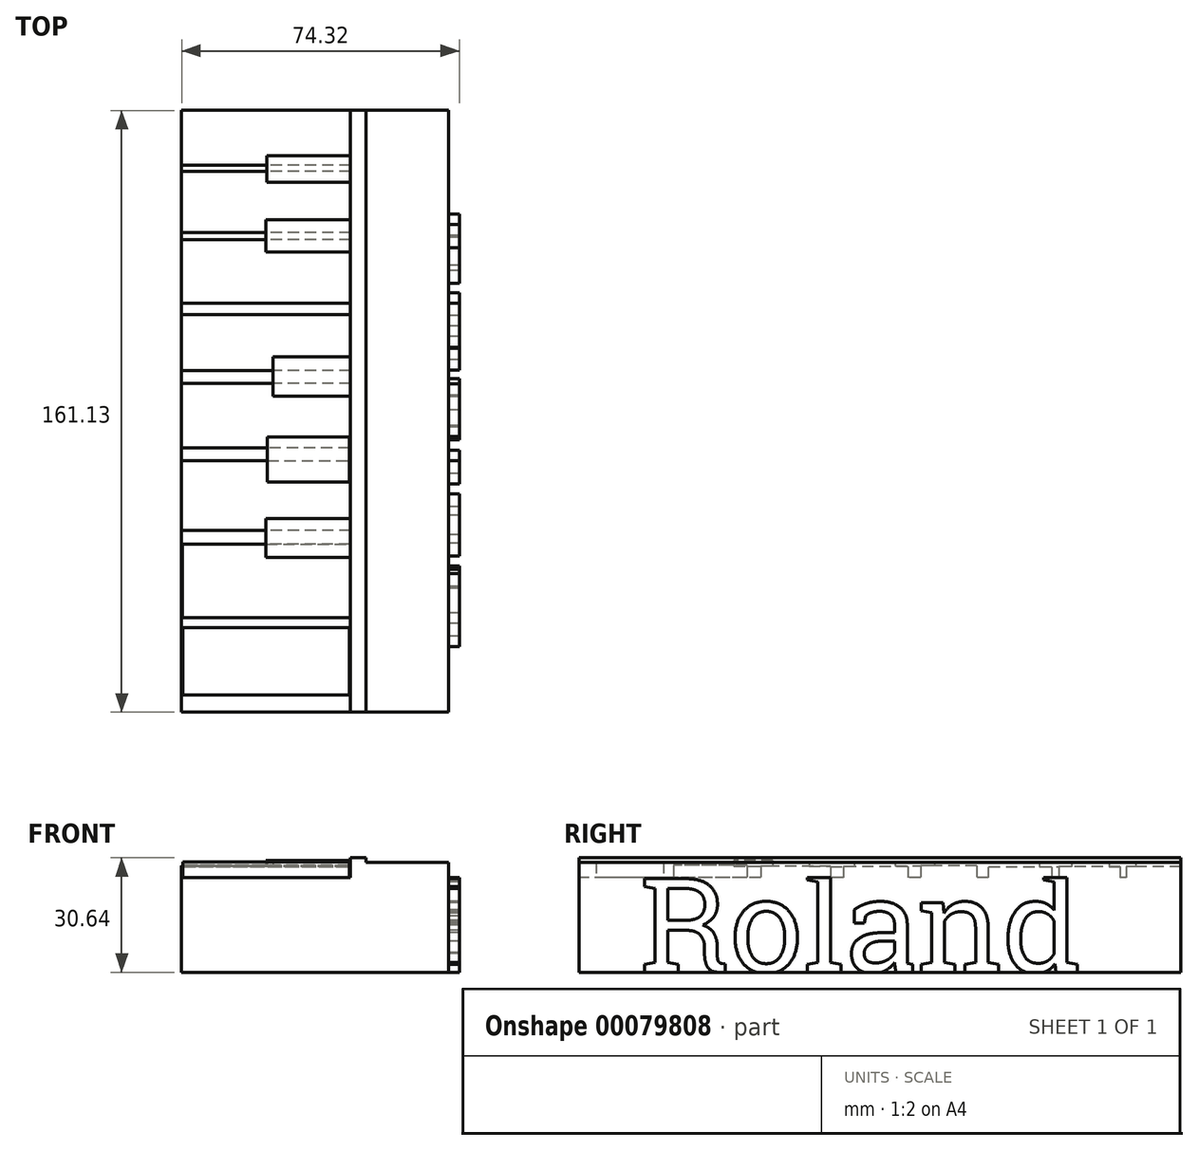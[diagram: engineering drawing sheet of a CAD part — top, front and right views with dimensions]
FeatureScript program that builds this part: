
annotation { "Feature Type Name" : "Feature", "Feature Type Description" : "" }
export const myFeature = defineFeature(function(context is Context, id is Id, definition is map)
    precondition{}
    {
        {
            var Q0;
            Q0=qCreatedBy(makeId("Top.planeOp"),FACE);
            var sketch = newSketch(context, id + "F0", { "sketchPlane" : qUnion([Q0])});
            skLineSegment(sketch, "E0.bottom", {"start": v(-39.3, 62.64) * mm, "end": v(32.17, 62.64) * mm});
            skLineSegment(sketch, "E0.top", {"start": v(-39.3, -98.49) * mm, "end": v(32.17, -98.49) * mm});
            skLineSegment(sketch, "E0.left", {"start": v(-39.3, 62.64) * mm, "end": v(-39.3, -98.49) * mm});
            skLineSegment(sketch, "E0.right", {"start": v(32.17, 62.64) * mm, "end": v(32.17, -98.49) * mm});
            skSolve(sketch);
        }
        {
            var Q0;
            Q0=makeQuery(id+"F0.imprint","IMPRINT",FACE,{"disambiguationData":[TD([[makeQuery(id+"F0.imprint","IMPRINT",EDGE,{"derivedFrom":sQuery(id+"F0.wireOp",EDGE,"E0.bottom")}),-1.0]])]});
            extrude(context, id + "F1", {"entities" : qUnion([Q0]), "depth" : 25.4 * mm});
        }
        {
            var Q0;
            Q0=makeQuery(id+"F1.opExtrude","CAP_FACE",FACE,{"disambiguationData":[OSD([sQuery(id+"F0.wireOp",EDGE,"E0.bottom"),sQuery(id+"F0.wireOp",EDGE,"E0.top"),sQuery(id+"F0.wireOp",EDGE,"E0.left"),sQuery(id+"F0.wireOp",EDGE,"E0.right")])],"isStart":false});
            var sketch = newSketch(context, id + "F2", { "sketchPlane" : qUnion([Q0])});
            skLineSegment(sketch, "E1.bottom", {"start": v(10.06, 62.64) * mm, "end": v(5.9, 62.64) * mm});
            skLineSegment(sketch, "E1.top", {"start": v(10.06, -98.49) * mm, "end": v(5.9, -98.49) * mm});
            skLineSegment(sketch, "E1.left", {"start": v(10.06, 62.64) * mm, "end": v(10.06, -98.49) * mm});
            skLineSegment(sketch, "E1.right", {"start": v(5.9, 62.64) * mm, "end": v(5.9, -98.49) * mm});
            skSolve(sketch);
        }
        {
            var Q0;
            Q0=makeQuery(id+"F2.imprint","IMPRINT",FACE,{"disambiguationData":[TD([[makeQuery(id+"F2.imprint","IMPRINT",EDGE,{"derivedFrom":sQuery(id+"F2.wireOp",EDGE,"E1.bottom")}),-1.0]])]});
            extrude(context, id + "F3", {"entities" : qUnion([Q0]), "operationType" : NewBodyOperationType.ADD, "depth" : 5.24 * mm});
        }
        {
            var Q0;
            {var subQ0=sQuery(id+"F0.wireOp",EDGE,"E0.left");var subQ1=sQuery(id+"F0.wireOp",EDGE,"E0.top");var subQ2=sQuery(id+"F0.wireOp",EDGE,"E0.bottom");Q0=makeQuery(id+"F3.boolean.opBoolean","SPLIT",FACE,{"disambiguationData":[TD([makeQuery(id+"F1.opExtrude","SWEPT_FACE",FACE,{"disambiguationData":[OSD([subQ0])]})])],"derivedFrom":makeQuery(id+"F1.opExtrude","CAP_FACE",FACE,{"disambiguationData":[OSD([subQ2,subQ1,subQ0,sQuery(id+"F0.wireOp",EDGE,"E0.right")])],"isStart":false})});}
            var sketch = newSketch(context, id + "F4", { "sketchPlane" : qUnion([Q0])});
            skLineSegment(sketch, "E2.bottom", {"start": v(5.9, 62.64) * mm, "end": v(-39.3, 62.64) * mm});
            skLineSegment(sketch, "E2.top", {"start": v(5.9, 47.98) * mm, "end": v(-39.3, 47.98) * mm});
            skLineSegment(sketch, "E2.left", {"start": v(5.9, 62.64) * mm, "end": v(5.9, 47.98) * mm});
            skLineSegment(sketch, "E2.right", {"start": v(-39.3, 62.64) * mm, "end": v(-39.3, 47.98) * mm});
            skSolve(sketch);
        }
        {
            var Q0;
            Q0=makeQuery(id+"F4.imprint","IMPRINT",FACE,{"disambiguationData":[TD([[makeQuery(id+"F4.imprint","IMPRINT",EDGE,{"derivedFrom":sQuery(id+"F4.wireOp",EDGE,"E2.bottom")}),-1.0]])]});
            extrude(context, id + "F5", {"entities" : qUnion([Q0]), "operationType" : NewBodyOperationType.ADD, "depth" : 2.9 * mm});
        }
        {
            var Q0;
            {var subQ0=sQuery(id+"F0.wireOp",EDGE,"E0.left");var subQ1=sQuery(id+"F0.wireOp",EDGE,"E0.top");var subQ2=sQuery(id+"F0.wireOp",EDGE,"E0.bottom");Q0=makeQuery(id+"F3.boolean.opBoolean","SPLIT",FACE,{"disambiguationData":[TD([makeQuery(id+"F1.opExtrude","SWEPT_FACE",FACE,{"disambiguationData":[OSD([subQ0])]})])],"derivedFrom":makeQuery(id+"F1.opExtrude","CAP_FACE",FACE,{"disambiguationData":[OSD([subQ2,subQ1,subQ0,sQuery(id+"F0.wireOp",EDGE,"E0.right")])],"isStart":false})});}
            var sketch = newSketch(context, id + "F6", { "sketchPlane" : qUnion([Q0])});
            skLineSegment(sketch, "E3.bottom", {"start": v(5.9, 46.37) * mm, "end": v(-39.3, 46.37) * mm});
            skLineSegment(sketch, "E3.top", {"start": v(5.9, 30) * mm, "end": v(-39.3, 30) * mm});
            skLineSegment(sketch, "E3.left", {"start": v(5.9, 46.37) * mm, "end": v(5.9, 30) * mm});
            skLineSegment(sketch, "E3.right", {"start": v(-39.3, 46.37) * mm, "end": v(-39.3, 30) * mm});
            skSolve(sketch);
        }
        {
            var Q0;
            Q0=makeQuery(id+"F6.imprint","IMPRINT",FACE,{"disambiguationData":[TD([[makeQuery(id+"F6.imprint","IMPRINT",EDGE,{"derivedFrom":sQuery(id+"F6.wireOp",EDGE,"E3.bottom")}),1.0]])]});
            extrude(context, id + "F7", {"entities" : qUnion([Q0]), "operationType" : NewBodyOperationType.ADD, "depth" : 2.86 * mm});
        }
        {
            var Q0;
            Q0=makeQuery(id+"F5.opExtrude","CAP_FACE",FACE,{"disambiguationData":[OSD([sQuery(id+"F4.wireOp",EDGE,"E2.bottom"),sQuery(id+"F4.wireOp",EDGE,"E2.top"),sQuery(id+"F4.wireOp",EDGE,"E2.left"),sQuery(id+"F4.wireOp",EDGE,"E2.right")])],"isStart":false});
            var sketch = newSketch(context, id + "F8", { "sketchPlane" : qUnion([Q0])});
            skLineSegment(sketch, "E4.bottom", {"start": v(5.9, 50.54) * mm, "end": v(-16.48, 50.54) * mm});
            skLineSegment(sketch, "E4.top", {"start": v(5.9, 43.8) * mm, "end": v(-16.48, 43.8) * mm});
            skLineSegment(sketch, "E4.left", {"start": v(5.9, 50.54) * mm, "end": v(5.9, 43.8) * mm});
            skLineSegment(sketch, "E4.right", {"start": v(-16.48, 50.54) * mm, "end": v(-16.48, 43.8) * mm});
            skSolve(sketch);
        }
        {
            var Q0;
            {var subQ0=sQuery(id+"F8.wireOp",EDGE,"E4.bottom");Q0=makeQuery(id+"F8.imprint","IMPRINT",FACE,{"disambiguationData":[TD([[makeQuery(id+"F8.imprint","IMPRINT",EDGE,{"derivedFrom":subQ0}),1.0]])]});}
            extrude(context, id + "F9", {"entities" : qUnion([Q0]), "operationType" : NewBodyOperationType.ADD, "depth" : 1 * mm});
        }
        {
            var Q0;
            {var subQ0=sQuery(id+"F4.wireOp",EDGE,"E2.top");Q0=makeQuery(id+"F9.boolean.opBoolean","MERGE",FACE,{"derivedFrom":[makeQuery(id+"F5.opExtrude","SWEPT_FACE",FACE,{"disambiguationData":[OSD([subQ0])]}),makeQuery(id+"F9.opExtrude","SWEPT_FACE",FACE,{"disambiguationData":[OSD([subQ0])]})]});}
            var sketch = newSketch(context, id + "F10", { "sketchPlane" : qUnion([Q0])});
            skLineSegment(sketch, "E5.bottom", {"start": v(5.9, 29.3) * mm, "end": v(-16.48, 29.3) * mm});
            skLineSegment(sketch, "E5.top", {"start": v(5.9, 28.3) * mm, "end": v(-16.48, 28.3) * mm});
            skLineSegment(sketch, "E5.left", {"start": v(5.9, 29.3) * mm, "end": v(5.9, 28.3) * mm});
            skLineSegment(sketch, "E5.right", {"start": v(-16.48, 29.3) * mm, "end": v(-16.48, 28.3) * mm});
            skSolve(sketch);
        }
        {
            var Q0;
            Q0=makeQuery(id+"F10.imprint","IMPRINT",FACE,{"disambiguationData":[TD([[makeQuery(id+"F10.imprint","IMPRINT",EDGE,{"derivedFrom":sQuery(id+"F10.wireOp",EDGE,"E5.bottom")}),1.0]])]});
            extrude(context, id + "F11", {"entities" : qUnion([Q0]), "operationType" : NewBodyOperationType.ADD, "depth" : 4.6 * mm});
        }
        {
            var Q0;
            {var subQ2=sQuery(id+"F0.wireOp",EDGE,"E0.left");var subQ3=makeQuery(id+"F1.opExtrude","SWEPT_FACE",FACE,{"disambiguationData":[OSD([subQ2])]});var subQ4=sQuery(id+"F0.wireOp",EDGE,"E0.top");var subQ5=makeQuery(id+"F1.opExtrude","SWEPT_FACE",FACE,{"disambiguationData":[OSD([subQ4])]});var subQ6=sQuery(id+"F0.wireOp",EDGE,"E0.bottom");Q0=makeQuery(id+"F7.boolean.opBoolean","SPLIT",FACE,{"disambiguationData":[TD([subQ5])],"derivedFrom":makeQuery(id+"F3.boolean.opBoolean","SPLIT",FACE,{"disambiguationData":[TD([subQ3])],"derivedFrom":makeQuery(id+"F1.opExtrude","CAP_FACE",FACE,{"disambiguationData":[OSD([subQ6,subQ4,subQ2,sQuery(id+"F0.wireOp",EDGE,"E0.right")])],"isStart":false})})});}
            var sketch = newSketch(context, id + "F12", { "sketchPlane" : qUnion([Q0])});
            skLineSegment(sketch, "E6.bottom", {"start": v(5.9, 28) * mm, "end": v(-39.3, 28) * mm});
            skLineSegment(sketch, "E6.top", {"start": v(5.9, 11.05) * mm, "end": v(-39.3, 11.05) * mm});
            skLineSegment(sketch, "E6.left", {"start": v(5.9, 28) * mm, "end": v(5.9, 11.05) * mm});
            skLineSegment(sketch, "E6.right", {"start": v(-39.3, 28) * mm, "end": v(-39.3, 11.05) * mm});
            skSolve(sketch);
        }
        {
            var Q0;
            Q0=makeQuery(id+"F12.imprint","IMPRINT",FACE,{"disambiguationData":[TD([[makeQuery(id+"F12.imprint","IMPRINT",EDGE,{"derivedFrom":sQuery(id+"F12.wireOp",EDGE,"E6.bottom")}),1.0]])]});
            extrude(context, id + "F13", {"entities" : qUnion([Q0]), "operationType" : NewBodyOperationType.ADD, "depth" : 2.72 * mm});
        }
        {
            var Q0;
            Q0=makeQuery(id+"F7.opExtrude","CAP_FACE",FACE,{"disambiguationData":[OSD([sQuery(id+"F6.wireOp",EDGE,"E3.bottom"),sQuery(id+"F6.wireOp",EDGE,"E3.top"),sQuery(id+"F6.wireOp",EDGE,"E3.left"),sQuery(id+"F6.wireOp",EDGE,"E3.right")])],"isStart":false});
            var sketch = newSketch(context, id + "F14", { "sketchPlane" : qUnion([Q0])});
            skLineSegment(sketch, "E7.bottom", {"start": v(5.9, 33.31) * mm, "end": v(-16.7, 33.31) * mm});
            skLineSegment(sketch, "E7.top", {"start": v(5.9, 30) * mm, "end": v(-16.7, 30) * mm});
            skLineSegment(sketch, "E7.left", {"start": v(5.9, 33.31) * mm, "end": v(5.9, 30) * mm});
            skLineSegment(sketch, "E7.right", {"start": v(-16.7, 33.31) * mm, "end": v(-16.7, 30) * mm});
            skSolve(sketch);
        }
        {
            var Q0;
            Q0=makeQuery(id+"F14.imprint","IMPRINT",FACE,{"disambiguationData":[TD([[makeQuery(id+"F14.imprint","IMPRINT",EDGE,{"derivedFrom":sQuery(id+"F14.wireOp",EDGE,"E7.bottom")}),1.0]])]});
            extrude(context, id + "F15", {"entities" : qUnion([Q0]), "operationType" : NewBodyOperationType.ADD, "depth" : 0.97 * mm});
        }
        {
            var Q0;
            Q0=makeQuery(id+"F15.boolean.opBoolean","MERGE",FACE,{"derivedFrom":[makeQuery(id+"F7.opExtrude","SWEPT_FACE",FACE,{"disambiguationData":[OSD([sQuery(id+"F6.wireOp",EDGE,"E3.top")])]}),makeQuery(id+"F15.opExtrude","SWEPT_FACE",FACE,{"disambiguationData":[OSD([sQuery(id+"F14.wireOp",EDGE,"E7.top")])]})]});
            var sketch = newSketch(context, id + "F16", { "sketchPlane" : qUnion([Q0])});
            skLineSegment(sketch, "E8.bottom", {"start": v(5.9, 29.23) * mm, "end": v(-16.7, 29.23) * mm});
            skLineSegment(sketch, "E8.top", {"start": v(5.9, 28.26) * mm, "end": v(-16.7, 28.26) * mm});
            skLineSegment(sketch, "E8.left", {"start": v(5.9, 29.23) * mm, "end": v(5.9, 28.26) * mm});
            skLineSegment(sketch, "E8.right", {"start": v(-16.7, 29.23) * mm, "end": v(-16.7, 28.26) * mm});
            skSolve(sketch);
        }
        {
            var Q0;
            Q0=makeQuery(id+"F16.imprint","IMPRINT",FACE,{"disambiguationData":[TD([[makeQuery(id+"F16.imprint","IMPRINT",EDGE,{"derivedFrom":sQuery(id+"F16.wireOp",EDGE,"E8.bottom")}),1.0]])]});
            extrude(context, id + "F17", {"entities" : qUnion([Q0]), "operationType" : NewBodyOperationType.ADD, "depth" : 5.23 * mm});
        }
        {
            var Q0;
            {var subQ3=sQuery(id+"F0.wireOp",EDGE,"E0.left");var subQ4=makeQuery(id+"F1.opExtrude","SWEPT_FACE",FACE,{"disambiguationData":[OSD([subQ3])]});var subQ6=sQuery(id+"F0.wireOp",EDGE,"E0.top");var subQ7=makeQuery(id+"F1.opExtrude","SWEPT_FACE",FACE,{"disambiguationData":[OSD([subQ6])]});var subQ8=sQuery(id+"F0.wireOp",EDGE,"E0.bottom");Q0=makeQuery(id+"F13.boolean.opBoolean","SPLIT",FACE,{"disambiguationData":[TD([subQ7])],"derivedFrom":makeQuery(id+"F7.boolean.opBoolean","SPLIT",FACE,{"disambiguationData":[TD([subQ7])],"derivedFrom":makeQuery(id+"F3.boolean.opBoolean","SPLIT",FACE,{"disambiguationData":[TD([subQ4])],"derivedFrom":makeQuery(id+"F1.opExtrude","CAP_FACE",FACE,{"disambiguationData":[OSD([subQ8,subQ6,subQ3,sQuery(id+"F0.wireOp",EDGE,"E0.right")])],"isStart":false})})})});}
            var sketch = newSketch(context, id + "F18", { "sketchPlane" : qUnion([Q0])});
            skLineSegment(sketch, "E9.bottom", {"start": v(5.9, 7.96) * mm, "end": v(-39.3, 7.96) * mm});
            skLineSegment(sketch, "E9.top", {"start": v(5.9, -7.06) * mm, "end": v(-39.3, -7.06) * mm});
            skLineSegment(sketch, "E9.left", {"start": v(5.9, 7.96) * mm, "end": v(5.9, -7.06) * mm});
            skLineSegment(sketch, "E9.right", {"start": v(-39.3, 7.96) * mm, "end": v(-39.3, -7.06) * mm});
            skSolve(sketch);
        }
        {
            var Q0;
            Q0=makeQuery(id+"F18.imprint","IMPRINT",FACE,{"disambiguationData":[TD([[makeQuery(id+"F18.imprint","IMPRINT",EDGE,{"derivedFrom":sQuery(id+"F18.wireOp",EDGE,"E9.bottom")}),1.0]])]});
            extrude(context, id + "F19", {"entities" : qUnion([Q0]), "operationType" : NewBodyOperationType.ADD, "depth" : 3.12 * mm});
        }
        {
            var Q0;
            {var subQ3=sQuery(id+"F0.wireOp",EDGE,"E0.left");var subQ4=makeQuery(id+"F1.opExtrude","SWEPT_FACE",FACE,{"disambiguationData":[OSD([subQ3])]});var subQ6=sQuery(id+"F0.wireOp",EDGE,"E0.top");var subQ7=makeQuery(id+"F1.opExtrude","SWEPT_FACE",FACE,{"disambiguationData":[OSD([subQ6])]});var subQ9=sQuery(id+"F0.wireOp",EDGE,"E0.bottom");Q0=makeQuery(id+"F19.boolean.opBoolean","SPLIT",FACE,{"disambiguationData":[TD([subQ7])],"derivedFrom":makeQuery(id+"F13.boolean.opBoolean","SPLIT",FACE,{"disambiguationData":[TD([subQ7])],"derivedFrom":makeQuery(id+"F7.boolean.opBoolean","SPLIT",FACE,{"disambiguationData":[TD([subQ7])],"derivedFrom":makeQuery(id+"F3.boolean.opBoolean","SPLIT",FACE,{"disambiguationData":[TD([subQ4])],"derivedFrom":makeQuery(id+"F1.opExtrude","CAP_FACE",FACE,{"disambiguationData":[OSD([subQ9,subQ6,subQ3,sQuery(id+"F0.wireOp",EDGE,"E0.right")])],"isStart":false})})})})});}
            var sketch = newSketch(context, id + "F20", { "sketchPlane" : qUnion([Q0])});
            skLineSegment(sketch, "E10.bottom", {"start": v(5.9, -10.45) * mm, "end": v(-39.3, -10.45) * mm});
            skLineSegment(sketch, "E10.top", {"start": v(5.9, -27.7) * mm, "end": v(-39.3, -27.7) * mm});
            skLineSegment(sketch, "E10.left", {"start": v(5.9, -10.45) * mm, "end": v(5.9, -27.7) * mm});
            skLineSegment(sketch, "E10.right", {"start": v(-39.3, -10.45) * mm, "end": v(-39.3, -27.7) * mm});
            skSolve(sketch);
        }
        {
            var Q0;
            Q0=makeQuery(id+"F20.imprint","IMPRINT",FACE,{"disambiguationData":[TD([[makeQuery(id+"F20.imprint","IMPRINT",EDGE,{"derivedFrom":sQuery(id+"F20.wireOp",EDGE,"E10.bottom")}),1.0]])]});
            extrude(context, id + "F21", {"entities" : qUnion([Q0]), "operationType" : NewBodyOperationType.ADD, "depth" : 2.84 * mm});
        }
        {
            var Q0;
            Q0=makeQuery(id+"F19.opExtrude","CAP_FACE",FACE,{"disambiguationData":[OSD([sQuery(id+"F18.wireOp",EDGE,"E9.bottom"),sQuery(id+"F18.wireOp",EDGE,"E9.top"),sQuery(id+"F18.wireOp",EDGE,"E9.left"),sQuery(id+"F18.wireOp",EDGE,"E9.right")])],"isStart":false});
            var sketch = newSketch(context, id + "F22", { "sketchPlane" : qUnion([Q0])});
            skLineSegment(sketch, "E11.bottom", {"start": v(5.9, -3.38) * mm, "end": v(-14.8, -3.38) * mm});
            skLineSegment(sketch, "E11.top", {"start": v(5.9, -7.06) * mm, "end": v(-14.8, -7.06) * mm});
            skLineSegment(sketch, "E11.left", {"start": v(5.9, -3.38) * mm, "end": v(5.9, -7.06) * mm});
            skLineSegment(sketch, "E11.right", {"start": v(-14.8, -3.38) * mm, "end": v(-14.8, -7.06) * mm});
            skSolve(sketch);
        }
        {
            var Q0;
            Q0=makeQuery(id+"F22.imprint","IMPRINT",FACE,{"disambiguationData":[TD([[makeQuery(id+"F22.imprint","IMPRINT",EDGE,{"derivedFrom":sQuery(id+"F22.wireOp",EDGE,"E11.bottom")}),1.0]])]});
            extrude(context, id + "F23", {"entities" : qUnion([Q0]), "operationType" : NewBodyOperationType.ADD, "depth" : 1.01 * mm});
        }
        {
            var Q0;
            Q0=makeQuery(id+"F23.boolean.opBoolean","MERGE",FACE,{"derivedFrom":[makeQuery(id+"F19.opExtrude","SWEPT_FACE",FACE,{"disambiguationData":[OSD([sQuery(id+"F18.wireOp",EDGE,"E9.top")])]}),makeQuery(id+"F23.opExtrude","SWEPT_FACE",FACE,{"disambiguationData":[OSD([sQuery(id+"F22.wireOp",EDGE,"E11.top")])]})]});
            var sketch = newSketch(context, id + "F24", { "sketchPlane" : qUnion([Q0])});
            skLineSegment(sketch, "E12.bottom", {"start": v(5.9, 29.53) * mm, "end": v(-14.8, 29.53) * mm});
            skLineSegment(sketch, "E12.top", {"start": v(5.9, 28.52) * mm, "end": v(-14.8, 28.52) * mm});
            skLineSegment(sketch, "E12.left", {"start": v(5.9, 29.53) * mm, "end": v(5.9, 28.52) * mm});
            skLineSegment(sketch, "E12.right", {"start": v(-14.8, 29.53) * mm, "end": v(-14.8, 28.52) * mm});
            skSolve(sketch);
        }
        {
            var Q0;
            Q0=makeQuery(id+"F24.imprint","IMPRINT",FACE,{"disambiguationData":[TD([[makeQuery(id+"F24.imprint","IMPRINT",EDGE,{"derivedFrom":sQuery(id+"F24.wireOp",EDGE,"E12.bottom")}),1.0]])]});
            extrude(context, id + "F25", {"entities" : qUnion([Q0]), "operationType" : NewBodyOperationType.ADD, "depth" : 6.76 * mm});
        }
        {
            var Q0;
            {var subQ3=sQuery(id+"F0.wireOp",EDGE,"E0.left");var subQ4=makeQuery(id+"F1.opExtrude","SWEPT_FACE",FACE,{"disambiguationData":[OSD([subQ3])]});var subQ6=sQuery(id+"F0.wireOp",EDGE,"E0.top");var subQ7=makeQuery(id+"F1.opExtrude","SWEPT_FACE",FACE,{"disambiguationData":[OSD([subQ6])]});var subQ10=sQuery(id+"F0.wireOp",EDGE,"E0.bottom");Q0=makeQuery(id+"F21.boolean.opBoolean","SPLIT",FACE,{"disambiguationData":[TD([subQ7])],"derivedFrom":makeQuery(id+"F19.boolean.opBoolean","SPLIT",FACE,{"disambiguationData":[TD([subQ7])],"derivedFrom":makeQuery(id+"F13.boolean.opBoolean","SPLIT",FACE,{"disambiguationData":[TD([subQ7])],"derivedFrom":makeQuery(id+"F7.boolean.opBoolean","SPLIT",FACE,{"disambiguationData":[TD([subQ7])],"derivedFrom":makeQuery(id+"F3.boolean.opBoolean","SPLIT",FACE,{"disambiguationData":[TD([subQ4])],"derivedFrom":makeQuery(id+"F1.opExtrude","CAP_FACE",FACE,{"disambiguationData":[OSD([subQ10,subQ6,subQ3,sQuery(id+"F0.wireOp",EDGE,"E0.right")])],"isStart":false})})})})})});}
            var sketch = newSketch(context, id + "F26", { "sketchPlane" : qUnion([Q0])});
            skLineSegment(sketch, "E13.bottom", {"start": v(5.9, -31.1) * mm, "end": v(-39.3, -31.1) * mm});
            skLineSegment(sketch, "E13.top", {"start": v(5.9, -49.8) * mm, "end": v(-39.3, -49.8) * mm});
            skLineSegment(sketch, "E13.left", {"start": v(5.9, -31.1) * mm, "end": v(5.9, -49.8) * mm});
            skLineSegment(sketch, "E13.right", {"start": v(-39.3, -31.1) * mm, "end": v(-39.3, -49.8) * mm});
            skSolve(sketch);
        }
        {
            var Q0;
            Q0=makeQuery(id+"F26.imprint","IMPRINT",FACE,{"disambiguationData":[TD([[makeQuery(id+"F26.imprint","IMPRINT",EDGE,{"derivedFrom":sQuery(id+"F26.wireOp",EDGE,"E13.bottom")}),1.0]])]});
            extrude(context, id + "F27", {"entities" : qUnion([Q0]), "operationType" : NewBodyOperationType.ADD, "depth" : 3.02 * mm});
        }
        {
            var Q0;
            Q0=makeQuery(id+"F21.opExtrude","CAP_FACE",FACE,{"disambiguationData":[OSD([sQuery(id+"F20.wireOp",EDGE,"E10.bottom"),sQuery(id+"F20.wireOp",EDGE,"E10.top"),sQuery(id+"F20.wireOp",EDGE,"E10.left"),sQuery(id+"F20.wireOp",EDGE,"E10.right")])],"isStart":false});
            var sketch = newSketch(context, id + "F28", { "sketchPlane" : qUnion([Q0])});
            skSolve(sketch);
        }
        {
            var Q0;
            Q0=makeQuery(id+"F28.imprint","IMPRINT",FACE,{"disambiguationData":[TD([[makeQuery(id+"F28.imprint","IMPRINT",EDGE,{"derivedFrom":makeQuery(id+"F21.opExtrude","CAP_EDGE",EDGE,{"disambiguationData":[OSD([sQuery(id+"F20.wireOp",EDGE,"E10.bottom")])],"isStart":false})}),1.0]])]});
            var sketch = newSketch(context, id + "F29", { "sketchPlane" : qUnion([Q0])});
            skLineSegment(sketch, "E14.bottom", {"start": v(5.63, -24.78) * mm, "end": v(-16.34, -24.78) * mm});
            skLineSegment(sketch, "E14.top", {"start": v(5.63, -27.53) * mm, "end": v(-16.34, -27.53) * mm});
            skLineSegment(sketch, "E14.left", {"start": v(5.63, -24.78) * mm, "end": v(5.63, -27.53) * mm});
            skLineSegment(sketch, "E14.right", {"start": v(-16.34, -24.78) * mm, "end": v(-16.34, -27.53) * mm});
            skSolve(sketch);
        }
        {
            var Q0;
            Q0=makeQuery(id+"F29.imprint","IMPRINT",FACE,{"disambiguationData":[TD([[makeQuery(id+"F29.imprint","IMPRINT",EDGE,{"derivedFrom":sQuery(id+"F29.wireOp",EDGE,"E14.bottom")}),1.0]])]});
            extrude(context, id + "F30", {"entities" : qUnion([Q0]), "operationType" : NewBodyOperationType.ADD, "depth" : 1.2 * mm});
        }
        {
            var Q0;
            Q0=makeQuery(id+"F30.opExtrude","SWEPT_FACE",FACE,{"disambiguationData":[OSD([sQuery(id+"F29.wireOp",EDGE,"E14.top")])]});
            extrude(context, id + "F31", {"entities" : qUnion([Q0]), "operationType" : NewBodyOperationType.ADD, "depth" : 9.34 * mm});
        }
        {
            var Q0;
            {var subQ2=sQuery(id+"F0.wireOp",EDGE,"E0.top");var subQ3=makeQuery(id+"F1.opExtrude","SWEPT_FACE",FACE,{"disambiguationData":[OSD([subQ2])]});var subQ6=sQuery(id+"F0.wireOp",EDGE,"E0.left");var subQ7=makeQuery(id+"F1.opExtrude","SWEPT_FACE",FACE,{"disambiguationData":[OSD([subQ6])]});var subQ11=sQuery(id+"F0.wireOp",EDGE,"E0.bottom");Q0=makeQuery(id+"F27.boolean.opBoolean","SPLIT",FACE,{"disambiguationData":[TD([subQ3])],"derivedFrom":makeQuery(id+"F21.boolean.opBoolean","SPLIT",FACE,{"disambiguationData":[TD([subQ3])],"derivedFrom":makeQuery(id+"F19.boolean.opBoolean","SPLIT",FACE,{"disambiguationData":[TD([subQ3])],"derivedFrom":makeQuery(id+"F13.boolean.opBoolean","SPLIT",FACE,{"disambiguationData":[TD([subQ3])],"derivedFrom":makeQuery(id+"F7.boolean.opBoolean","SPLIT",FACE,{"disambiguationData":[TD([subQ3])],"derivedFrom":makeQuery(id+"F3.boolean.opBoolean","SPLIT",FACE,{"disambiguationData":[TD([subQ7])],"derivedFrom":makeQuery(id+"F1.opExtrude","CAP_FACE",FACE,{"disambiguationData":[OSD([subQ11,subQ2,subQ6,sQuery(id+"F0.wireOp",EDGE,"E0.right")])],"isStart":false})})})})})})});}
            var sketch = newSketch(context, id + "F32", { "sketchPlane" : qUnion([Q0])});
            skSolve(sketch);
        }
        {
            var Q0;
            {var subQ9=sQuery(id+"F26.wireOp",EDGE,"E13.top");Q0=makeQuery(id+"F32.imprint","IMPRINT",FACE,{"disambiguationData":[TD([[makeQuery(id+"F32.imprint","IMPRINT",EDGE,{"derivedFrom":makeQuery(id+"F27.opExtrude","CAP_EDGE",EDGE,{"disambiguationData":[OSD([subQ9])],"isStart":true})}),1.0]])]});}
            var sketch = newSketch(context, id + "F33", { "sketchPlane" : qUnion([Q0])});
            skLineSegment(sketch, "E15.bottom", {"start": v(5.81, -53.5) * mm, "end": v(-39.04, -53.5) * mm});
            skLineSegment(sketch, "E15.top", {"start": v(5.81, -73.21) * mm, "end": v(-39.04, -73.21) * mm});
            skLineSegment(sketch, "E15.left", {"start": v(5.81, -53.5) * mm, "end": v(5.81, -73.21) * mm});
            skLineSegment(sketch, "E15.right", {"start": v(-39.04, -53.5) * mm, "end": v(-39.04, -73.21) * mm});
            skSolve(sketch);
        }
        {
            var Q0;
            Q0=makeQuery(id+"F33.imprint","IMPRINT",FACE,{"disambiguationData":[TD([[makeQuery(id+"F33.imprint","IMPRINT",EDGE,{"derivedFrom":sQuery(id+"F33.wireOp",EDGE,"E15.bottom")}),1.0]])]});
            extrude(context, id + "F34", {"entities" : qUnion([Q0]), "operationType" : NewBodyOperationType.ADD, "depth" : 3.25 * mm});
        }
        {
            var Q0;
            Q0=makeQuery(id+"F27.opExtrude","CAP_FACE",FACE,{"disambiguationData":[OSD([sQuery(id+"F26.wireOp",EDGE,"E13.bottom"),sQuery(id+"F26.wireOp",EDGE,"E13.top"),sQuery(id+"F26.wireOp",EDGE,"E13.left"),sQuery(id+"F26.wireOp",EDGE,"E13.right")])],"isStart":false});
            var sketch = newSketch(context, id + "F35", { "sketchPlane" : qUnion([Q0])});
            skLineSegment(sketch, "E16.bottom", {"start": v(5.9, -46.63) * mm, "end": v(-16.7, -46.63) * mm});
            skLineSegment(sketch, "E16.top", {"start": v(5.9, -49.8) * mm, "end": v(-16.7, -49.8) * mm});
            skLineSegment(sketch, "E16.left", {"start": v(5.9, -46.63) * mm, "end": v(5.9, -49.8) * mm});
            skLineSegment(sketch, "E16.right", {"start": v(-16.7, -46.63) * mm, "end": v(-16.7, -49.8) * mm});
            skSolve(sketch);
        }
        {
            var Q0;
            Q0=makeQuery(id+"F35.imprint","IMPRINT",FACE,{"disambiguationData":[TD([[makeQuery(id+"F35.imprint","IMPRINT",EDGE,{"derivedFrom":sQuery(id+"F35.wireOp",EDGE,"E16.bottom")}),1.0]])]});
            extrude(context, id + "F36", {"entities" : qUnion([Q0]), "operationType" : NewBodyOperationType.ADD, "depth" : 1.45 * mm});
        }
        {
            var Q0;
            Q0=makeQuery(id+"F36.boolean.opBoolean","MERGE",FACE,{"derivedFrom":[makeQuery(id+"F27.opExtrude","SWEPT_FACE",FACE,{"disambiguationData":[OSD([sQuery(id+"F26.wireOp",EDGE,"E13.top")])]}),makeQuery(id+"F36.opExtrude","SWEPT_FACE",FACE,{"disambiguationData":[OSD([sQuery(id+"F35.wireOp",EDGE,"E16.top")])]})]});
            var sketch = newSketch(context, id + "F37", { "sketchPlane" : qUnion([Q0])});
            skLineSegment(sketch, "E17.bottom", {"start": v(5.9, 29.88) * mm, "end": v(-16.7, 29.88) * mm});
            skLineSegment(sketch, "E17.top", {"start": v(5.9, 28.42) * mm, "end": v(-16.7, 28.42) * mm});
            skLineSegment(sketch, "E17.left", {"start": v(5.9, 29.88) * mm, "end": v(5.9, 28.42) * mm});
            skLineSegment(sketch, "E17.right", {"start": v(-16.7, 29.88) * mm, "end": v(-16.7, 28.42) * mm});
            skSolve(sketch);
        }
        {
            var Q0;
            Q0=makeQuery(id+"F37.imprint","IMPRINT",FACE,{"disambiguationData":[TD([[makeQuery(id+"F37.imprint","IMPRINT",EDGE,{"derivedFrom":sQuery(id+"F37.wireOp",EDGE,"E17.bottom")}),1.0]])]});
            extrude(context, id + "F38", {"entities" : qUnion([Q0]), "operationType" : NewBodyOperationType.ADD, "depth" : 7.24 * mm});
        }
        {
            var Q0;
            {var subQ9=sQuery(id+"F26.wireOp",EDGE,"E13.top");Q0=makeQuery(id+"F32.imprint","IMPRINT",FACE,{"disambiguationData":[TD([[makeQuery(id+"F32.imprint","IMPRINT",EDGE,{"derivedFrom":makeQuery(id+"F27.opExtrude","CAP_EDGE",EDGE,{"disambiguationData":[OSD([subQ9])],"isStart":true})}),1.0]])]});}
            var sketch = newSketch(context, id + "F39", { "sketchPlane" : qUnion([Q0])});
            skLineSegment(sketch, "E18.bottom", {"start": v(5.55, -75.86) * mm, "end": v(-38.97, -75.86) * mm});
            skLineSegment(sketch, "E18.top", {"start": v(5.55, -93.9) * mm, "end": v(-38.97, -93.9) * mm});
            skLineSegment(sketch, "E18.left", {"start": v(5.55, -75.86) * mm, "end": v(5.55, -93.9) * mm});
            skLineSegment(sketch, "E18.right", {"start": v(-38.97, -75.86) * mm, "end": v(-38.97, -93.9) * mm});
            skSolve(sketch);
        }
        {
            var Q0;
            Q0=makeQuery(id+"F39.imprint","IMPRINT",FACE,{"disambiguationData":[TD([[makeQuery(id+"F39.imprint","IMPRINT",EDGE,{"derivedFrom":sQuery(id+"F39.wireOp",EDGE,"E18.bottom")}),1.0]])]});
            extrude(context, id + "F40", {"entities" : qUnion([Q0]), "operationType" : NewBodyOperationType.ADD, "depth" : 4.12 * mm});
        }
        {
            var Q0;
            Q0=makeQuery(id+"F1.opExtrude","SWEPT_FACE",FACE,{"disambiguationData":[OSD([sQuery(id+"F0.wireOp",EDGE,"E0.right")])]});
            var sketch = newSketch(context, id + "F41", { "sketchPlane" : qUnion([Q0])});
            skText(sketch, "E19", { "text": "Roland", "fontName": "RobotoSlab-Regular.ttf"});
            const initialGuessF41  = {"E19": [-0.08211, 0, 1, 0, 0.0254]};
            skSetInitialGuess(sketch, initialGuessF41);
            skSolve(sketch);
        }
        {
            var Q0;
            {var subQ0=sQuery(id+"F0.wireOp",EDGE,"E0.right");var subQ1=sQuery(id+"F0.wireOp",EDGE,"E0.top");var subQ2=sQuery(id+"F0.wireOp",EDGE,"E0.bottom");Q0=makeQuery(id+"F3.boolean.opBoolean","SPLIT",FACE,{"disambiguationData":[TD([makeQuery(id+"F1.opExtrude","SWEPT_FACE",FACE,{"disambiguationData":[OSD([subQ0])]})])],"derivedFrom":makeQuery(id+"F1.opExtrude","CAP_FACE",FACE,{"disambiguationData":[OSD([subQ2,subQ1,sQuery(id+"F0.wireOp",EDGE,"E0.left"),subQ0])],"isStart":false})});}
            extrude(context, id + "F42", {"entities" : qUnion([Q0]), "operationType" : NewBodyOperationType.ADD, "depth" : 4.07 * mm});
        }
        {
            var Q0;
            {var subQ0=sQuery(id+"F41.wireOp",EDGE,"E19.sketch_text.stroke-59");Q0=makeQuery(id+"F41.imprint","IMPRINT",FACE,{"disambiguationData":[TD([[makeQuery(id+"F41.imprint","IMPRINT",EDGE,{"derivedFrom":subQ0}),-1.0]])]});}
            var Q1;
            {var subQ14=sQuery(id+"F41.wireOp",EDGE,"E19.sketch_text.stroke-127");Q1=makeQuery(id+"F41.imprint","IMPRINT",FACE,{"disambiguationData":[TD([[makeQuery(id+"F41.imprint","IMPRINT",EDGE,{"derivedFrom":subQ14}),-1.0]])]});}
            var Q2;
            Q2=makeQuery(id+"F41.imprint","IMPRINT",FACE,{"disambiguationData":[TD([[makeQuery(id+"F41.imprint","IMPRINT",EDGE,{"derivedFrom":sQuery(id+"F41.wireOp",EDGE,"E19.sketch_text.stroke-0")}),-1.0]])]});
            var Q3;
            Q3=makeQuery(id+"F41.imprint","IMPRINT",FACE,{"disambiguationData":[TD([[makeQuery(id+"F41.imprint","IMPRINT",EDGE,{"derivedFrom":sQuery(id+"F41.wireOp",EDGE,"E19.sketch_text.stroke-36")}),-1.0]])]});
            var Q4;
            Q4=makeQuery(id+"F41.imprint","IMPRINT",FACE,{"disambiguationData":[TD([[makeQuery(id+"F41.imprint","IMPRINT",EDGE,{"derivedFrom":sQuery(id+"F41.wireOp",EDGE,"E19.sketch_text.stroke-66")}),-1.0]])]});
            var Q5;
            Q5=makeQuery(id+"F41.imprint","IMPRINT",FACE,{"disambiguationData":[TD([[makeQuery(id+"F41.imprint","IMPRINT",EDGE,{"derivedFrom":sQuery(id+"F41.wireOp",EDGE,"E19.sketch_text.stroke-101")}),-1.0]])]});
            extrude(context, id + "F43", {"entities" : qUnion([Q0, Q1, Q2, Q3, Q4, Q5]), "operationType" : NewBodyOperationType.ADD, "depth" : 2.86 * mm});
        }
    });
